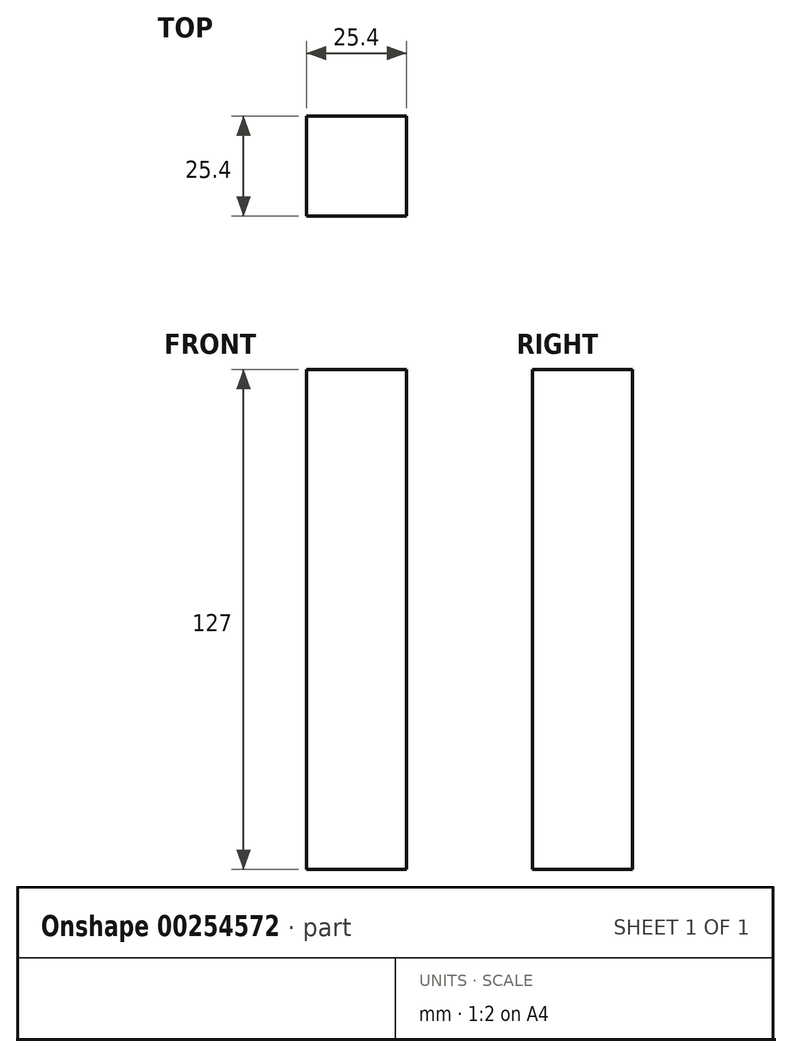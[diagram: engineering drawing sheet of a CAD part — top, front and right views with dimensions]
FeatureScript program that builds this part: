
annotation { "Feature Type Name" : "Feature", "Feature Type Description" : "" }
export const myFeature = defineFeature(function(context is Context, id is Id, definition is map)
    precondition{}
    {
        {
            var Q0;
            Q0=qCreatedBy(makeId("Top.planeOp"),FACE);
            var sketch = newSketch(context, id + "F0", { "sketchPlane" : qUnion([Q0])});
            skLineSegment(sketch, "E0.bottom", {"start": v(-38.18, 43.67) * mm, "end": v(-63.58, 43.67) * mm});
            skLineSegment(sketch, "E0.top", {"start": v(-38.18, 18.27) * mm, "end": v(-63.58, 18.27) * mm});
            skLineSegment(sketch, "E0.left", {"start": v(-38.18, 43.67) * mm, "end": v(-38.18, 18.27) * mm});
            skLineSegment(sketch, "E0.right", {"start": v(-63.58, 43.67) * mm, "end": v(-63.58, 18.27) * mm});
            skPoint(sketch, "E0.middle", {"position": v(-50.88, 30.97) * mm});
            skLineSegment(sketch, "E1.bottom", {"start": v(12.7, 43.67) * mm, "end": v(-12.7, 43.67) * mm});
            skLineSegment(sketch, "E1.top", {"start": v(12.7, 18.27) * mm, "end": v(-12.7, 18.27) * mm});
            skLineSegment(sketch, "E1.left", {"start": v(12.7, 43.67) * mm, "end": v(12.7, 18.27) * mm});
            skLineSegment(sketch, "E1.right", {"start": v(-12.7, 43.67) * mm, "end": v(-12.7, 18.27) * mm});
            skPoint(sketch, "E1.middle", {"position": v(0, 30.97) * mm});
            skLineSegment(sketch, "E2", {"start": v(-50.88, 30.97) * mm, "end": v(-0.08, 30.97) * mm});
            skLineSegment(sketch, "E3", {"start": v(0, 30.97) * mm, "end": v(50.8, 30.97) * mm});
            skPoint(sketch, "E3.endSnap0", {"position": v(12.7, 30.97) * mm});
            skLineSegment(sketch, "E4.bottom", {"start": v(63.5, 43.67) * mm, "end": v(38.1, 43.67) * mm});
            skLineSegment(sketch, "E4.top", {"start": v(63.5, 18.27) * mm, "end": v(38.1, 18.27) * mm});
            skLineSegment(sketch, "E4.left", {"start": v(63.5, 43.67) * mm, "end": v(63.5, 18.27) * mm});
            skLineSegment(sketch, "E4.right", {"start": v(38.1, 43.67) * mm, "end": v(38.1, 18.27) * mm});
            skPoint(sketch, "E4.middle", {"position": v(50.8, 30.97) * mm});
            skSolve(sketch);
        }
        {
            var Q0;
            Q0=makeQuery(id+"F0.imprint","IMPRINT",FACE,{"disambiguationData":[TD([[makeQuery(id+"F0.imprint","IMPRINT",EDGE,{"derivedFrom":sQuery(id+"F0.wireOp",EDGE,"E0.bottom")}),1.0]])]});
            extrude(context, id + "F1", {"entities" : qUnion([Q0]), "depth" : 63.5 * mm});
        }
        {
            var Q0;
            Q0=makeQuery(id+"F1.opExtrude","CAP_FACE",FACE,{"disambiguationData":[OSD([sQuery(id+"F0.wireOp",EDGE,"E0.bottom"),sQuery(id+"F0.wireOp",EDGE,"E0.top"),sQuery(id+"F0.wireOp",EDGE,"E0.left"),sQuery(id+"F0.wireOp",EDGE,"E0.right")])],"isStart":true});
            extrude(context, id + "F2", {"entities" : qUnion([Q0]), "operationType" : NewBodyOperationType.ADD, "depth" : 63.5 * mm});
        }
    });
